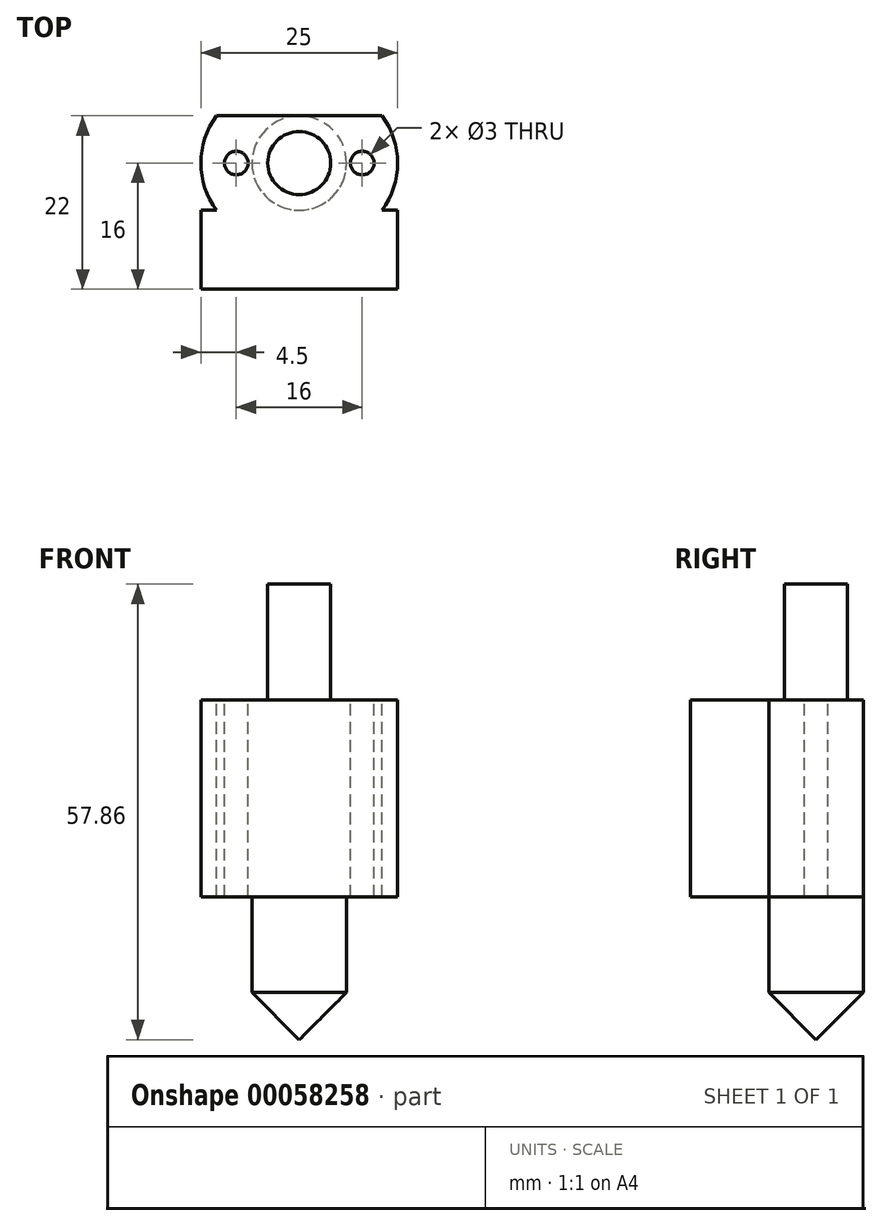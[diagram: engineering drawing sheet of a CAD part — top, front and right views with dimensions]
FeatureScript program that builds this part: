
annotation { "Feature Type Name" : "Feature", "Feature Type Description" : "" }
export const myFeature = defineFeature(function(context is Context, id is Id, definition is map)
    precondition{}
    {
        {
            var Q0;
            Q0=qCreatedBy(makeId("Front.planeOp"),FACE);
            var sketch = newSketch(context, id + "F0", { "sketchPlane" : qUnion([Q0])});
            skLineSegment(sketch, "E0.bottom", {"start": v(12.5, 12.5) * mm, "end": v(-12.5, 12.5) * mm});
            skLineSegment(sketch, "E0.top", {"start": v(12.5, -12.5) * mm, "end": v(-12.5, -12.5) * mm});
            skLineSegment(sketch, "E0.left", {"start": v(12.5, 12.5) * mm, "end": v(12.5, -12.5) * mm});
            skLineSegment(sketch, "E0.right", {"start": v(-12.5, 12.5) * mm, "end": v(-12.5, -12.5) * mm});
            skPoint(sketch, "E0.middle", {"position": v(0, 0) * mm});
            skSolve(sketch);
        }
        {
            var Q0;
            Q0 = qSketchRegion(id + "F0", true);
            extrude(context, id + "F1", {"entities" : qUnion([Q0]), "depth" : 10 * mm});
        }
        {
            var Q0;
            Q0=makeQuery(id+"F1.opExtrude","SWEPT_FACE",FACE,{"disambiguationData":[OSD([sQuery(id+"F0.wireOp",EDGE,"E0.bottom")])]});
            var sketch = newSketch(context, id + "F2", { "sketchPlane" : qUnion([Q0])});
            skLineSegment(sketch, "E1", {"start": v(0, 0) * mm, "end": v(0, 6) * mm, "construction": true});
            skLineSegment(sketch, "E2", {"start": v(0, 6) * mm, "end": v(-8, 6) * mm, "construction": true});
            skCircle(sketch, "E3", {"center": v(-8, 6) * mm, "radius": 1.5 * mm});
            skCircle(sketch, "E4.MirrorC", {"center": v(8, 6) * mm, "radius": 1.5 * mm});
            skArc(sketch, "E5", {"start": v(-10.5, 12) * mm, "mid": v(-12.5, 6) * mm, "end": v(-10.5, 0) * mm});
            skPoint(sketch, "E6", {"position": v(-12.5, 6) * mm});
            skPoint(sketch, "E6.positionSnap0", {"position": v(-12.5, 6) * mm});
            skArc(sketch, "E7.MirrorCS", {"start": v(10.5, 12) * mm, "mid": v(12.5, 6) * mm, "end": v(10.5, 0) * mm});
            skLineSegment(sketch, "E8", {"start": v(-10.5, 12) * mm, "end": v(10.5, 12) * mm});
            skLineSegment(sketch, "E9", {"start": v(-10.5, 0) * mm, "end": v(10.5, 0) * mm});
            skSolve(sketch);
        }
        {
            var Q0;
            Q0 = qSketchRegion(id + "F2", true);
            extrude(context, id + "F3", {"entities" : qUnion([Q0]), "oppositeDirection" : true, "depth" : 25 * mm});
        }
        {
            var Q0;
            Q0=makeQuery(id+"F3.opExtrude","CAP_FACE",FACE,{"disambiguationData":[OSD([sQuery(id+"F2.wireOp",EDGE,"E3"),sQuery(id+"F2.wireOp",EDGE,"E4.MirrorC"),sQuery(id+"F2.wireOp",EDGE,"E5"),sQuery(id+"F2.wireOp",EDGE,"E7.MirrorCS"),sQuery(id+"F2.wireOp",EDGE,"E8"),sQuery(id+"F2.wireOp",EDGE,"E9")])],"isStart":true});
            var sketch = newSketch(context, id + "F4", { "sketchPlane" : qUnion([Q0])});
            skLineSegment(sketch, "E10", {"start": v(0, 0) * mm, "end": v(0, 12) * mm, "construction": true});
            skCircle(sketch, "E11", {"center": v(0, 6) * mm, "radius": 4 * mm});
            skSolve(sketch);
        }
        {
            var Q0;
            Q0 = qSketchRegion(id + "F4", true);
            extrude(context, id + "F5", {"entities" : qUnion([Q0]), "operationType" : NewBodyOperationType.ADD, "depth" : 14.7 * mm});
        }
        {
            var Q0;
            Q0=makeQuery(id+"F3.opExtrude","CAP_FACE",FACE,{"disambiguationData":[OSD([sQuery(id+"F2.wireOp",EDGE,"E3"),sQuery(id+"F2.wireOp",EDGE,"E4.MirrorC"),sQuery(id+"F2.wireOp",EDGE,"E5"),sQuery(id+"F2.wireOp",EDGE,"E7.MirrorCS"),sQuery(id+"F2.wireOp",EDGE,"E8"),sQuery(id+"F2.wireOp",EDGE,"E9")])],"isStart":false});
            var sketch = newSketch(context, id + "F6", { "sketchPlane" : qUnion([Q0])});
            skLineSegment(sketch, "E12", {"start": v(0, 0) * mm, "end": v(0, -12) * mm, "construction": true});
            skCircle(sketch, "E13", {"center": v(0, -6) * mm, "radius": 6 * mm});
            skSolve(sketch);
        }
        {
            var Q0;
            Q0 = qSketchRegion(id + "F6", true);
            extrude(context, id + "F7", {"entities" : qUnion([Q0]), "operationType" : NewBodyOperationType.ADD, "depth" : 18.16 * mm});
        }
        {
            var Q0;
            Q0=makeQuery(id+"F7.opExtrude","CAP_EDGE",EDGE,{"disambiguationData":[OSD([sQuery(id+"F6.wireOp",EDGE,"E13")])],"isStart":false});
            chamfer(context, id + "F8", {"entities" : qUnion([Q0]), "width" : 6 * mm, "tangentPropagation" : true});
        }
    });
